# Revit family: Electronics_Commercial-Audio_Biamp_USB-Switch_200
name_source: partatom
category: Communication Devices
units: mm (PartAtom-declared; Revit-internal decimal feet)

## family parameters
Cut with Voids When Loaded = No
Host = Face
Maintain Annotation Orientation = No
OmniClass Number = 23.85.10.14
OmniClass Title = Visual Information Systems
Part Type = Normal
Room Calculation Point = No
Round Connector Dimension = Use Diameter
Shared = No

## types (1)
- USB 200
    Altitude = 0-6,600 ft (0-2000m) MSL
    Apparent Load = 15 VA
    Compliance = CE Marked (Europe) RoHS Directive (Europe)
    Connector Description = 5V DC 15W
    Cooling = Convection
    Default Elevation = 4' - 0"
    Depth = 0' - 3 3/4"
    Description = USB 200 USB Switch
    Height = 0' - 0 29/32"
    Housing Material = Biamp - Plastic - White
    Humidity = 10-90% (non-condensing)
    Manufacturer = Biamp
    Max Power Consumption = 15 W
    Model = USB 200 USB Switch
    Number of Poles = 1
    Power Factor = 1
    Product Documentation Link = https://downloads.biamp.com
    Product Page URL = https://www.biamp.com
    Product data url = https://www.bimobject.com
    Temperature Range = 32-104° F (0-40° C)
    URL = https://www.biamp.com
    Voltage = 5 V
    Weight = 0.20 lbf
    Width = 0' - 2 17/32"

## geometry (parser evidence)
native form markers: Blend x2, Sweep x3
no freeform markers — native parametric forms only
